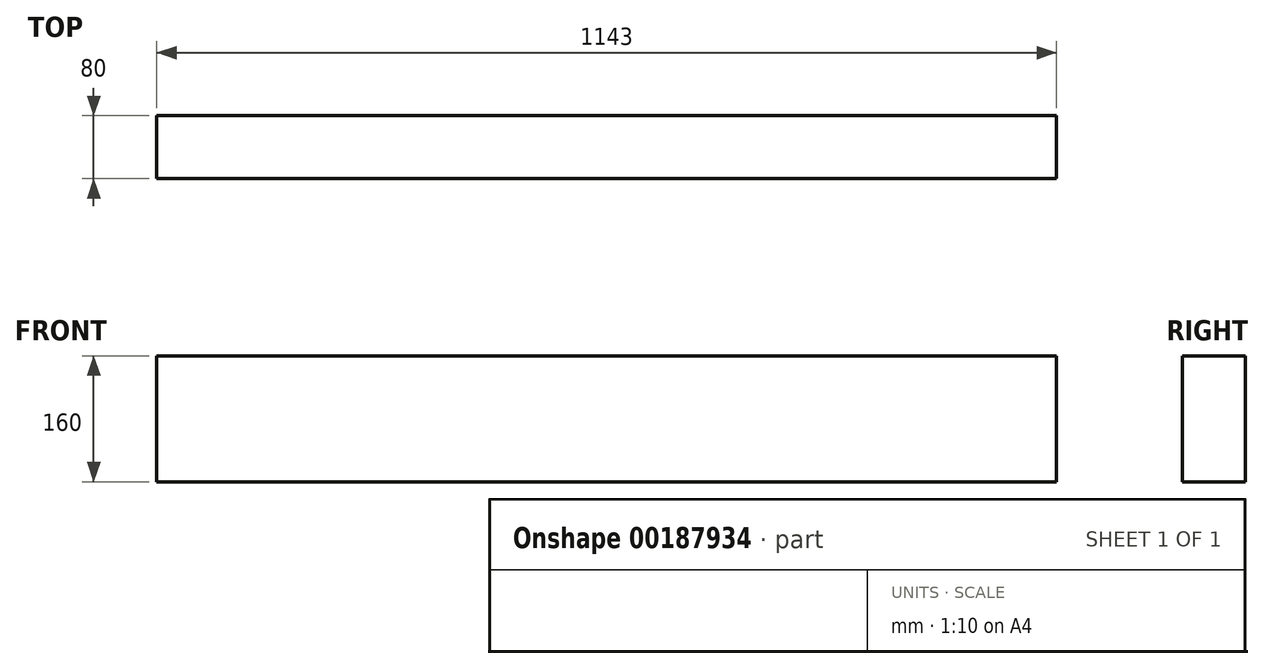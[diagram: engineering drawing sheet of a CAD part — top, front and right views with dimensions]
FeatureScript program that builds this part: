
annotation { "Feature Type Name" : "Feature", "Feature Type Description" : "" }
export const myFeature = defineFeature(function(context is Context, id is Id, definition is map)
    precondition{}
    {
        {
            var Q0;
            Q0=qCreatedBy(makeId("Front.planeOp"),FACE);
            var sketch = newSketch(context, id + "F0", { "sketchPlane" : qUnion([Q0])});
            skLineSegment(sketch, "E0.bottom", {"start": v(-568.07, 1.4) * mm, "end": v(574.93, 1.4) * mm});
            skLineSegment(sketch, "E0.top", {"start": v(-568.07, -158.6) * mm, "end": v(574.93, -158.6) * mm});
            skLineSegment(sketch, "E0.left", {"start": v(-568.07, 1.4) * mm, "end": v(-568.07, -158.6) * mm});
            skLineSegment(sketch, "E0.right", {"start": v(574.93, 1.4) * mm, "end": v(574.93, -158.6) * mm});
            skSolve(sketch);
        }
        {
            var Q0;
            Q0=makeQuery(id+"F0.imprint","IMPRINT",FACE,{"disambiguationData":[TD([[makeQuery(id+"F0.imprint","IMPRINT",EDGE,{"derivedFrom":sQuery(id+"F0.wireOp",EDGE,"E0.bottom")}),-1.0]])]});
            extrude(context, id + "F1", {"entities" : qUnion([Q0]), "depth" : 80 * mm});
        }
    });
